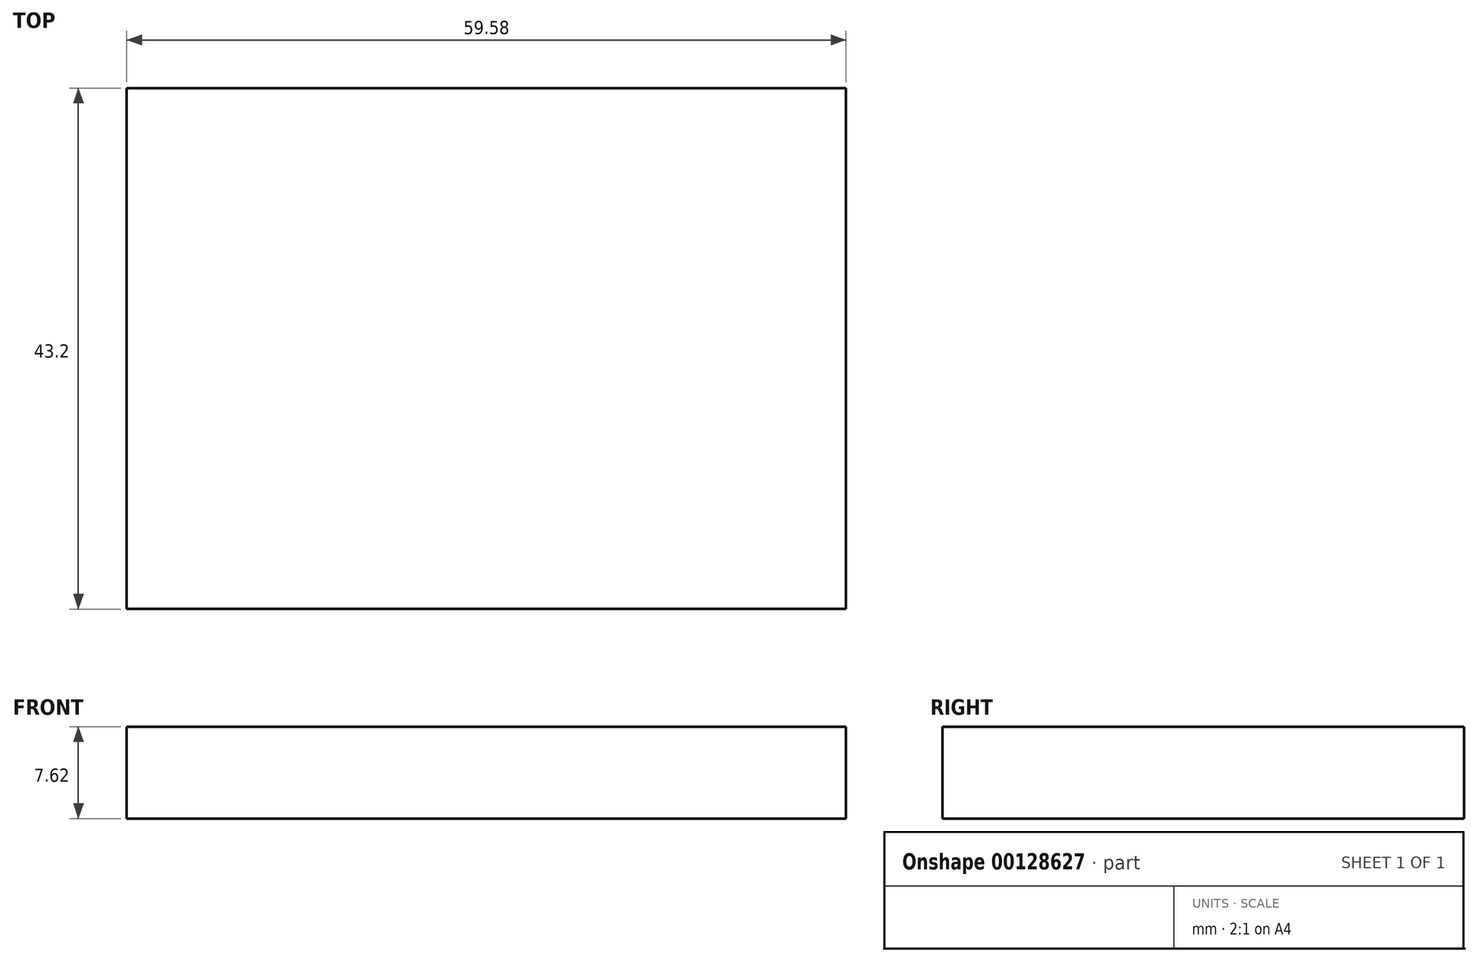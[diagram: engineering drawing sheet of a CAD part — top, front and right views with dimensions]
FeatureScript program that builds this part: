
annotation { "Feature Type Name" : "Feature", "Feature Type Description" : "" }
export const myFeature = defineFeature(function(context is Context, id is Id, definition is map)
    precondition{}
    {
        {
            var Q0;
            Q0=qCreatedBy(makeId("Top.planeOp"),FACE);
            var sketch = newSketch(context, id + "F0", { "sketchPlane" : qUnion([Q0])});
            skLineSegment(sketch, "E0.bottom", {"start": v(-30.41, 21.91) * mm, "end": v(29.17, 21.91) * mm});
            skLineSegment(sketch, "E0.top", {"start": v(-30.41, -21.29) * mm, "end": v(29.17, -21.29) * mm});
            skLineSegment(sketch, "E0.left", {"start": v(-30.41, 21.91) * mm, "end": v(-30.41, -21.29) * mm});
            skLineSegment(sketch, "E0.right", {"start": v(29.17, 21.91) * mm, "end": v(29.17, -21.29) * mm});
            skSolve(sketch);
        }
        {
            var Q0;
            Q0=makeQuery(id+"F0.imprint","IMPRINT",FACE,{"disambiguationData":[TD([[makeQuery(id+"F0.imprint","IMPRINT",EDGE,{"derivedFrom":sQuery(id+"F0.wireOp",EDGE,"E0.bottom")}),-1.0]])]});
            extrude(context, id + "F1", {"entities" : qUnion([Q0]), "depth" : 7.62 * mm});
        }
    });
